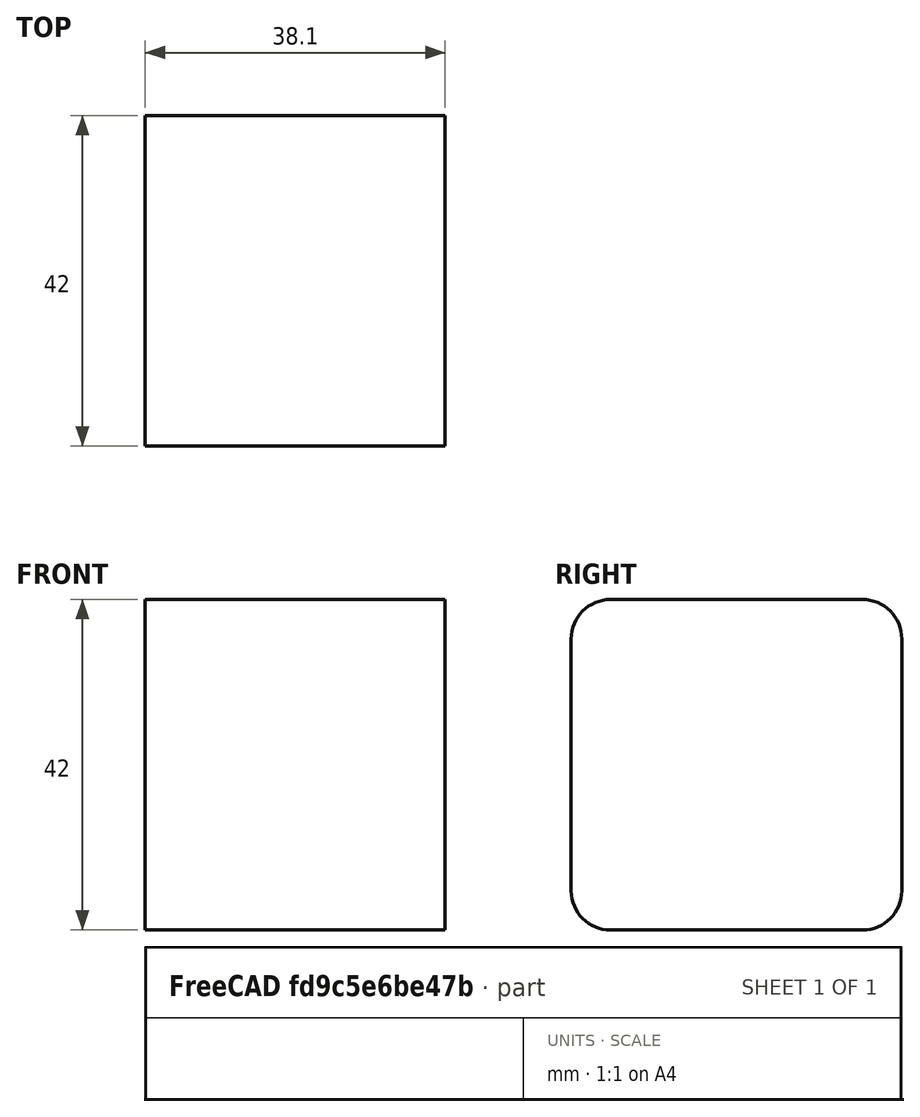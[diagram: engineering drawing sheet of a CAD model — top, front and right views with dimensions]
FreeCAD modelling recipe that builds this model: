
FCSTD DOCUMENT  (FreeCAD 1.1R40971 (Git))
Label: nema-17
License: All rights reserved
LicenseURL: http://en.wikipedia.org/wiki/All_rights_reserved
objects: Sketcher::SketchObject×1, App::Point×1, PartDesign::Pad×1, PartDesign::Body×1
note: 6 computed .brp shape members not serialized (recipe doc carries the construction recipe); baked Part::Feature solids carry a one-line shape summary decoded from their .brp

FEATURE [Sketcher::SketchObject] Sketch  label="smotor"
  ArcFitTolerance = 0
  ExternalTypes = [0]
  FullyConstrained = true
  MakeInternals = false
  MapMode = 5
  Placement = pos=(0,0,0) rot=(0.57735,0.57735,0.57735;2.0944rad)
  sketch-geometry (12):
    g0: LineSegment StartX=-16 StartY=21 StartZ=0 EndX=16 EndY=21 EndZ=0
    g1: LineSegment StartX=21 StartY=16 StartZ=0 EndX=21 EndY=-16 EndZ=0
    g2: LineSegment StartX=16 StartY=-21 StartZ=0 EndX=-16 EndY=-21 EndZ=0
    g3: LineSegment StartX=-21 StartY=-16 StartZ=0 EndX=-21 EndY=16 EndZ=0
    g4: ArcOfCircle CenterX=-16 CenterY=16 CenterZ=0 NormalX=0 NormalY=0 NormalZ=1 AngleXU=0 Radius=5 StartAngle=1.5708 EndAngle=3.14159
    g5: GeomPoint [constr] X=-21 Y=21 Z=0
    g6: ArcOfCircle CenterX=-16 CenterY=-16 CenterZ=0 NormalX=0 NormalY=0 NormalZ=1 AngleXU=0 Radius=5 StartAngle=3.14159 EndAngle=4.71239
    g7: GeomPoint [constr] X=-21 Y=-21 Z=0
    g8: ArcOfCircle CenterX=16 CenterY=-16 CenterZ=0 NormalX=0 NormalY=0 NormalZ=1 AngleXU=0 Radius=5 StartAngle=4.71239 EndAngle=6.28319
    g9: GeomPoint [constr] X=21 Y=-21 Z=0
    g10: ArcOfCircle CenterX=16 CenterY=16 CenterZ=0 NormalX=0 NormalY=0 NormalZ=1 AngleXU=0 Radius=5 StartAngle=0 EndAngle=1.5708
    g11: GeomPoint [constr] X=21 Y=21 Z=0
  constraints (26):
    c: Horizontal(g2)
    c: Vertical(g1)
    c: Symmetric(g11,g5,g-2)
    c: Symmetric(g5,g7,g-1)
    c: DistanceX(g5,g11) = 42
    c: PointOnObject(g5,g0)
    c: PointOnObject(g5,g3)
    c: Tangent(g0,g4) = 1.5708
    c: Tangent(g3,g4) = 1.5708
    c: PointOnObject(g7,g3)
    c: PointOnObject(g7,g2)
    c: Tangent(g3,g6) = 1.5708
    c: Tangent(g2,g6) = 1.5708
    c: PointOnObject(g9,g2)
    c: PointOnObject(g9,g1)
    c: Tangent(g2,g8) = 1.5708
    c: Tangent(g1,g8) = 1.5708
    c: PointOnObject(g11,g1)
    c: PointOnObject(g11,g0)
    c: Tangent(g1,g10) = 1.5708
    c: Tangent(g0,g10) = 1.5708
    c: Equal(g10,g8)
    c: Equal(g8,g6)
    c: Equal(g6,g4)
    c: Radius(g10) = 5
    c: Equal(g0,g3)
FEATURE [App::Point] Origin001  label="Origin"
  Role = Origin
FEATURE [PartDesign::Pad] Pad
  Direction = (1,0,0)
  Length = 38.1
  Length2 = 10
  Placement = pos=(0,0,0) rot=(1,1,1;2.0944rad)
  Profile = -> Sketch
  ReferenceAxis = -> Sketch [N_Axis]
  Suppressed = false
  Type = 0
FEATURE [PartDesign::Body] Body
  AllowCompound = false
  Group = -> [Sketch,Pad]
  Origin = -> Origin
  Tip = -> Pad
